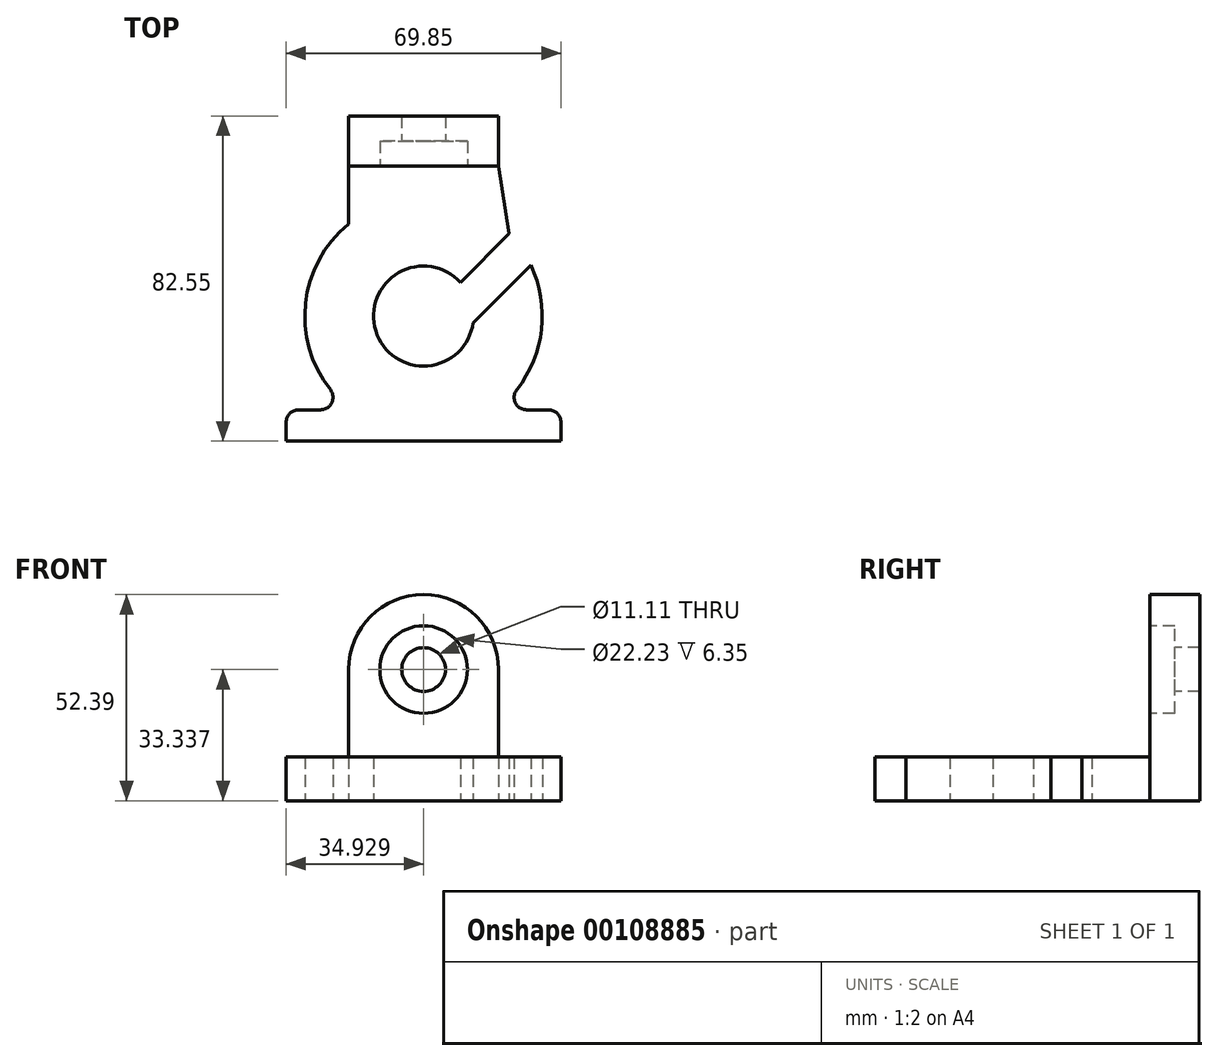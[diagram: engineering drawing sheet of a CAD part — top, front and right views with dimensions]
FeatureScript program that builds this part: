
annotation { "Feature Type Name" : "Feature", "Feature Type Description" : "" }
export const myFeature = defineFeature(function(context is Context, id is Id, definition is map)
    precondition{}
    {
        {
            var Q0;
            Q0=qCreatedBy(makeId("Top.planeOp"),FACE);
            var sketch = newSketch(context, id + "F0", { "sketchPlane" : qUnion([Q0])});
            skLineSegment(sketch, "E0.bottom", {"start": v(-32.79, -40.3) * mm, "end": v(-16.37, -40.3) * mm});
            skLineSegment(sketch, "E0.top", {"start": v(-32.79, -48.24) * mm, "end": v(37.06, -48.24) * mm});
            skLineSegment(sketch, "E0.left", {"start": v(-32.79, -40.3) * mm, "end": v(-32.79, -48.24) * mm});
            skLineSegment(sketch, "E0.right", {"start": v(37.06, -40.3) * mm, "end": v(37.06, -48.24) * mm});
            skArc(sketch, "E1", {"start": v(11.53, -7.93) * mm, "mid": v(-9.99, -20.26) * mm, "end": v(14.72, -18.2) * mm});
            skLineSegment(sketch, "E2.trimOffspring", {"start": v(20.65, -40.3) * mm, "end": v(37.06, -40.3) * mm});
            skArc(sketch, "E3.0", {"start": v(-16.91, 6.9) * mm, "mid": v(-4.5, -45.9) * mm, "end": v(29.38, -3.55) * mm});
            skLineSegment(sketch, "E4.bottom", {"start": v(-16.91, 21.61) * mm, "end": v(21.19, 21.61) * mm});
            skPoint(sketch, "E5", {"position": v(2.14, -48.24) * mm});
            skPoint(sketch, "E6", {"position": v(2.14, 21.61) * mm});
            skLineSegment(sketch, "E7", {"start": v(11.53, -7.93) * mm, "end": v(23.88, 4.42) * mm});
            skLineSegment(sketch, "E8", {"start": v(14.72, -18.2) * mm, "end": v(29.38, -3.55) * mm});
            skLineSegment(sketch, "E9", {"start": v(42.6, -20.65) * mm, "end": v(51.5, -20.65) * mm});
            skLineSegment(sketch, "E10.trimOffspring", {"start": v(23.88, 4.42) * mm, "end": v(23.88, 4.42) * mm});
            skLineSegment(sketch, "E11", {"start": v(-16.91, 21.61) * mm, "end": v(-16.91, 6.9) * mm});
            skLineSegment(sketch, "E12", {"start": v(21.19, 21.61) * mm, "end": v(23.88, 4.42) * mm});
            skLineSegment(sketch, "E13", {"start": v(-16.91, 21.61) * mm, "end": v(-16.91, 34.31) * mm});
            skLineSegment(sketch, "E14", {"start": v(-16.91, 34.31) * mm, "end": v(21.19, 34.31) * mm});
            skLineSegment(sketch, "E15", {"start": v(21.19, 34.31) * mm, "end": v(21.19, 21.61) * mm});
            skSolve(sketch);
        }
        {
            var Q0;
            Q0=makeQuery(id+"F0.imprint","IMPRINT",FACE,{"disambiguationData":[TD([[makeQuery(id+"F0.imprint","IMPRINT",EDGE,{"derivedFrom":sQuery(id+"F0.wireOp",EDGE,"E1")}),-1.0]])]});
            var Q1;
            Q1=makeQuery(id+"F0.imprint","IMPRINT",FACE,{"disambiguationData":[TD([[makeQuery(id+"F0.imprint","IMPRINT",EDGE,{"derivedFrom":sQuery(id+"F0.wireOp",EDGE,"E4.bottom")}),1.0]])]});
            var Q2;
            {var subQ0=sQuery(id+"F0.wireOp",EDGE,"E0.bottom");Q2=makeQuery(id+"F0.imprint","IMPRINT",FACE,{"disambiguationData":[TD([[makeQuery(id+"F0.imprint","IMPRINT",EDGE,{"derivedFrom":subQ0}),-1.0]])]});}
            extrude(context, id + "F1", {"entities" : qUnion([Q0, Q1, Q2]), "depth" : 11.1 * mm});
        }
        {
            var Q0;
            Q0=makeQuery(id+"F1.opExtrude","SWEPT_FACE",FACE,{"disambiguationData":[OSD([sQuery(id+"F0.wireOp",EDGE,"E14")])]});
            var sketch = newSketch(context, id + "F2", { "sketchPlane" : qUnion([Q0])});
            skLineSegment(sketch, "E16", {"start": v(-21.19, 11.11) * mm, "end": v(-21.19, 33.34) * mm});
            skLineSegment(sketch, "E17", {"start": v(-21.19, 33.34) * mm, "end": v(16.91, 33.34) * mm});
            skLineSegment(sketch, "E18", {"start": v(16.91, 33.34) * mm, "end": v(16.91, 11.11) * mm});
            skArc(sketch, "E19", {"start": v(16.91, 33.34) * mm, "mid": v(-2.14, 52.39) * mm, "end": v(-21.19, 33.34) * mm});
            skSolve(sketch);
        }
        {
            var Q0;
            Q0 = qSketchRegion(id + "F2", true);
            var Q1;
            Q1=makeQuery(id+"F2.imprint","IMPRINT",FACE,{"disambiguationData":[TD([[makeQuery(id+"F2.imprint","IMPRINT",EDGE,{"derivedFrom":sQuery(id+"F2.wireOp",EDGE,"E16")}),-1.0]])]});
            extrude(context, id + "F3", {"entities" : qUnion([Q0, Q1]), "operationType" : NewBodyOperationType.ADD, "oppositeDirection" : true, "depth" : 12.7 * mm});
        }
        {
            var Q0;
            Q0=makeQuery(id+"F3.opExtrude","CAP_FACE",FACE,{"disambiguationData":[OSD([sQuery(id+"F0.wireOp",EDGE,"E14"),sQuery(id+"F2.wireOp",EDGE,"E16"),sQuery(id+"F2.wireOp",EDGE,"E18"),sQuery(id+"F2.wireOp",EDGE,"E19")])],"isStart":false});
            var sketch = newSketch(context, id + "F4", { "sketchPlane" : qUnion([Q0])});
            skPoint(sketch, "E20", {"position": v(2.14, 33.34) * mm});
            skSolve(sketch);
        }
        {
            var Q0;
            Q0=sQuery(id+"F4.wireOp",VERTEX,"E20");
            var Q1;
            Q1=makeQuery(id+"F1.opExtrude","SWEPT_BODY",BODY,{"disambiguationData":[OSD([sQuery(id+"F0.wireOp",EDGE,"E0.bottom"),sQuery(id+"F0.wireOp",EDGE,"E0.top"),sQuery(id+"F0.wireOp",EDGE,"E0.left"),sQuery(id+"F0.wireOp",EDGE,"E0.right"),sQuery(id+"F0.wireOp",EDGE,"E1"),sQuery(id+"F0.wireOp",EDGE,"E2.trimOffspring"),sQuery(id+"F0.wireOp",EDGE,"E3.0"),sQuery(id+"F0.wireOp",EDGE,"E7"),sQuery(id+"F0.wireOp",EDGE,"E8"),sQuery(id+"F0.wireOp",EDGE,"E10.trimOffspring"),sQuery(id+"F0.wireOp",EDGE,"E11"),sQuery(id+"F0.wireOp",EDGE,"E12"),sQuery(id+"F0.wireOp",EDGE,"E13"),sQuery(id+"F0.wireOp",EDGE,"E14"),sQuery(id+"F0.wireOp",EDGE,"E15")])]});
            hole(context, id + "F5", {"style" : HoleStyle.C_BORE, "endStyle" : HoleEndStyle.BLIND, "holeDiameter" : 11.1 * mm, "cBoreDiameter" : 22.22 * mm, "cBoreDepth" : 6.35 * mm, "holeDepth" : 12.7 * mm, "startFromSketch" : true, "locations" : qUnion([Q0]), "scope" : qUnion([Q1])});
        }
        {
            var Q0;
            Q0=makeQuery(id+"F1.opExtrude","SWEPT_EDGE",EDGE,{"disambiguationData":[OSD([sQuery(id+"F0.wireOp",EDGE,"E0.right"),sQuery(id+"F0.wireOp",EDGE,"E2.trimOffspring")])]});
            var Q1;
            Q1=makeQuery(id+"F1.opExtrude","SWEPT_EDGE",EDGE,{"disambiguationData":[OSD([sQuery(id+"F0.wireOp",EDGE,"E2.trimOffspring"),sQuery(id+"F0.wireOp",EDGE,"E3.0")])]});
            var Q2;
            Q2=makeQuery(id+"F1.opExtrude","SWEPT_EDGE",EDGE,{"disambiguationData":[OSD([sQuery(id+"F0.wireOp",EDGE,"E0.bottom"),sQuery(id+"F0.wireOp",EDGE,"E3.0")])]});
            var Q3;
            Q3=makeQuery(id+"F1.opExtrude","SWEPT_EDGE",EDGE,{"disambiguationData":[OSD([sQuery(id+"F0.wireOp",EDGE,"E0.bottom"),sQuery(id+"F0.wireOp",EDGE,"E0.left")])]});
            fillet(context, id + "F6", {"entities" : qUnion([Q0, Q1, Q2, Q3]), "radius" : 3.17 * mm, "tangentPropagation" : true, "allowEdgeOverflow" : false});
        }
    });
